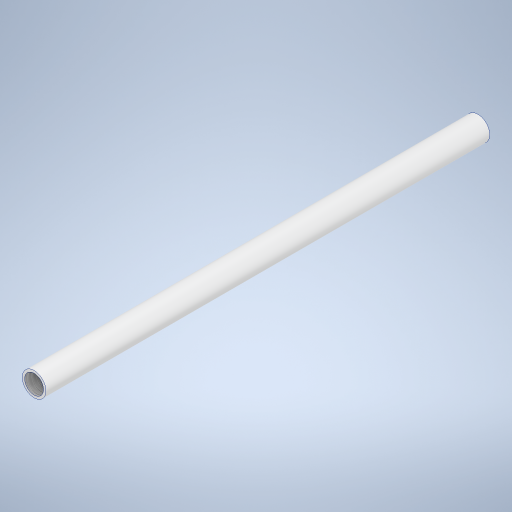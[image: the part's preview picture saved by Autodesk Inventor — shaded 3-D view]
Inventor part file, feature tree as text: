
AUTODESK INVENTOR PART (.ipt)
format: ipt  version: 2023 (Build 270158000, 158)  size: 249,856 bytes
history: native  units: mm
features: sketch x2, extrude x1, hole x1, thread x1
ambient origin geometry x8: Origin, YZ Plane, XZ Plane, XY Plane, X Axis, Y Axis, Z Axis, Center Point
bodies: Solid1 (feature_tree)
feature tree (5):
  extrude  "Extrusion1"  Depth=150.0mm TaperAngle=0.0deg
  hole  "Hole1"  [1 undecoded]
  thread  "Thread1"  [1 undecoded]
  sketch  "Sketch1"  dims[d0=8.0mm d1=150.0mm d2=0.0mm]
  sketch  "Sketch2"  dims[d3=6.35mm d4=6.0mm d5=3.023mm d6=2.0mm d7=14.3117mm d8=10.0mm d9=20.594885mm d10=15.103mm d11=0.0mm]
note: 2 required parameter values undecoded (feature->parameter linkage not recoverable at this tier; creation-order binding heuristic only, values carry confidence <= 0.55)
